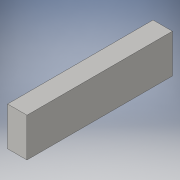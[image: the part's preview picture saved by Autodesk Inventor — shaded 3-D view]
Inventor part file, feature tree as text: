
AUTODESK INVENTOR PART (.ipt)
format: ipt  version: 2016 (Build 200138000, 138)  size: 87,040 bytes
history: native  units: in
note: dims shown in document units (in); Inventor stores cm internally (conversion verified against a paired STEP export)
features: extrude x1, sketch x1
ambient origin geometry x8: Origin, YZ Plane, XZ Plane, XY Plane, X Axis, Y Axis, Z Axis, Center Point
bodies: Solid1 (feature_tree)
feature tree (2):
  extrude  "Extrusion1"  Depth=4.0in
  sketch  "Sketch1"  dims[d0=2.0in d1=4.0in d2=15.0in d3=0.0in]
